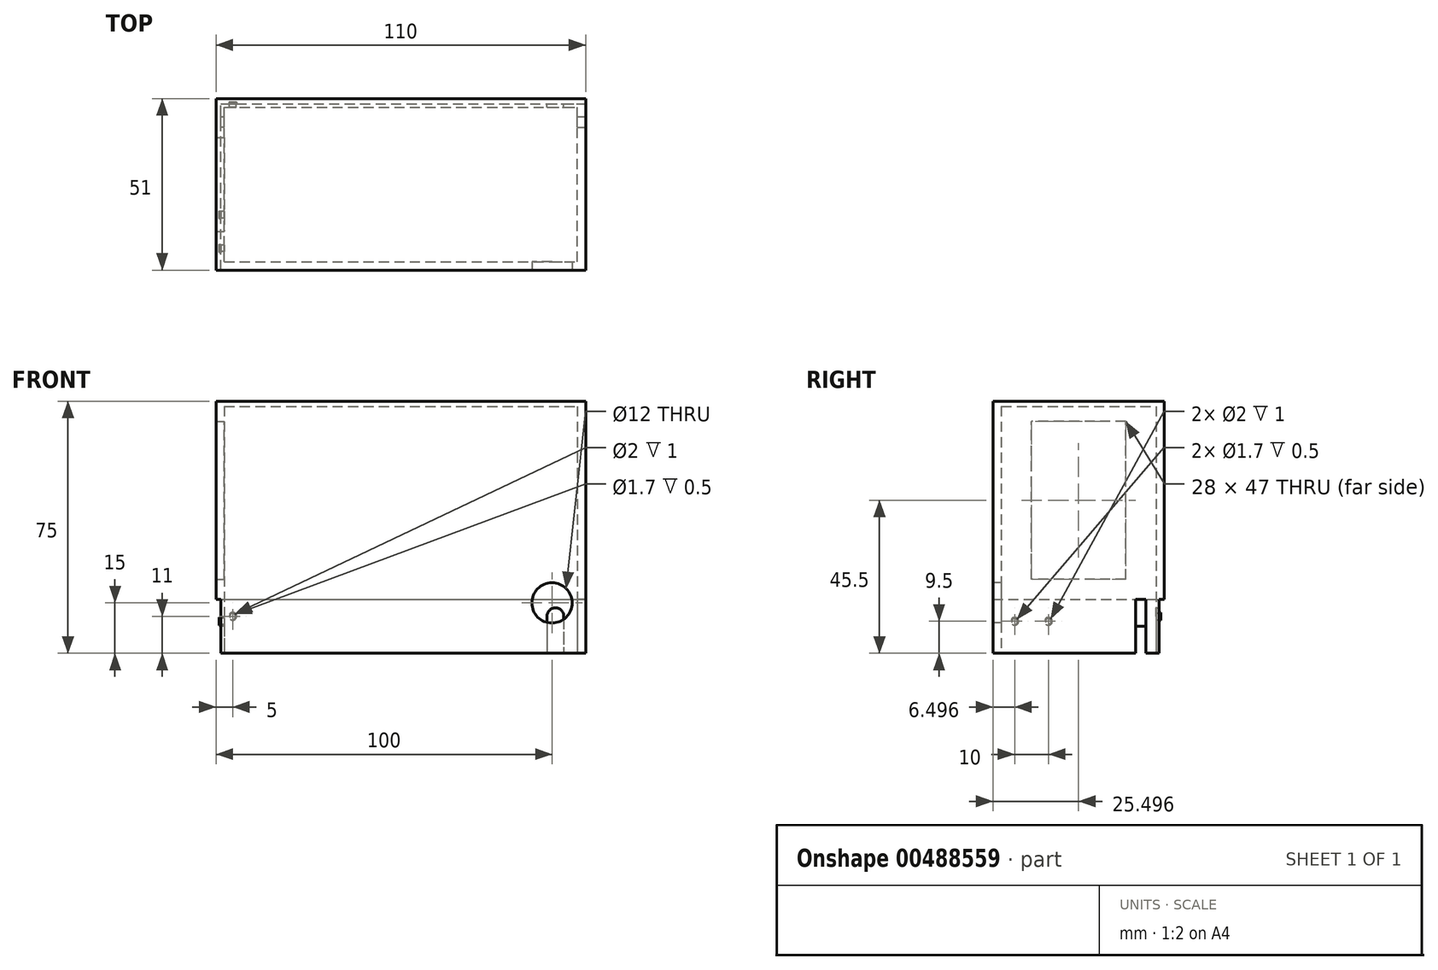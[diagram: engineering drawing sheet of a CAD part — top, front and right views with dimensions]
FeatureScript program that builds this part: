
annotation { "Feature Type Name" : "Feature", "Feature Type Description" : "" }
export const myFeature = defineFeature(function(context is Context, id is Id, definition is map)
    precondition{}
    {
        {
            var Q0;
            Q0=qCreatedBy(makeId("Top.planeOp"),FACE);
            var sketch = newSketch(context, id + "F0", { "sketchPlane" : qUnion([Q0])});
            skLineSegment(sketch, "E0.bottom", {"start": v(-40.86, -34.43) * mm, "end": v(69.14, -34.43) * mm});
            skLineSegment(sketch, "E0.top", {"start": v(-40.86, 16.57) * mm, "end": v(69.14, 16.57) * mm});
            skLineSegment(sketch, "E0.left", {"start": v(-40.86, -34.43) * mm, "end": v(-40.86, 16.57) * mm});
            skLineSegment(sketch, "E0.right", {"start": v(69.14, -34.43) * mm, "end": v(69.14, 16.57) * mm});
            skLineSegment(sketch, "E1.0", {"start": v(-38.36, -31.93) * mm, "end": v(-38.36, 14.07) * mm});
            skLineSegment(sketch, "E1.1", {"start": v(-38.36, -31.93) * mm, "end": v(66.64, -31.93) * mm});
            skLineSegment(sketch, "E1.2", {"start": v(66.64, -31.93) * mm, "end": v(66.64, 14.07) * mm});
            skLineSegment(sketch, "E1.3", {"start": v(-38.36, 14.07) * mm, "end": v(66.64, 14.07) * mm});
            skSolve(sketch);
        }
        {
            var Q0;
            Q0=makeQuery(id+"F0.imprint","IMPRINT",FACE,{"disambiguationData":[TD([[makeQuery(id+"F0.imprint","IMPRINT",EDGE,{"derivedFrom":sQuery(id+"F0.wireOp",EDGE,"E0.bottom")}),1.0]])]});
            extrude(context, id + "F1", {"entities" : qUnion([Q0]), "depth" : 75 * mm});
        }
        {
            var Q0;
            Q0=makeQuery(id+"F0.imprint","IMPRINT",FACE,{"disambiguationData":[TD([[makeQuery(id+"F0.imprint","IMPRINT",EDGE,{"derivedFrom":sQuery(id+"F0.wireOp",EDGE,"E0.bottom")}),1.0]])]});
            var sketch = newSketch(context, id + "F2", { "sketchPlane" : qUnion([Q0])});
            skLineSegment(sketch, "E2.0", {"start": v(-39.36, 15.07) * mm, "end": v(69.14, 15.07) * mm});
            skLineSegment(sketch, "E2.1", {"start": v(-39.36, -34.43) * mm, "end": v(-39.36, 15.07) * mm});
            skSolve(sketch);
        }
        {
            var Q0;
            {var subQ3=sQuery(id+"F2.wireOp",EDGE,"E2.0");Q0=makeQuery(id+"F2.imprint","IMPRINT",FACE,{"disambiguationData":[TD([[makeQuery(id+"F2.imprint","IMPRINT",EDGE,{"derivedFrom":subQ3}),1.0]])]});}
            extrude(context, id + "F3", {"entities" : qUnion([Q0]), "depth" : 16 * mm});
        }
        {
            var Q0;
            Q0=makeQuery(id+"F3.opExtrude","SWEPT_BODY",BODY,{"disambiguationData":[OSD([sQuery(id+"F0.wireOp",EDGE,"E0.bottom"),sQuery(id+"F0.wireOp",EDGE,"E0.top"),sQuery(id+"F0.wireOp",EDGE,"E0.left"),sQuery(id+"F0.wireOp",EDGE,"E0.right"),sQuery(id+"F2.wireOp",EDGE,"67fc0016-b919-42dd-8cfe-59e69e24b751.0"),sQuery(id+"F2.wireOp",EDGE,"67fc0016-b919-42dd-8cfe-59e69e24b751.1")])]});
            var Q1;
            Q1=makeQuery(id+"F1.opExtrude","SWEPT_BODY",BODY,{"disambiguationData":[OSD([sQuery(id+"F0.wireOp",EDGE,"E0.bottom"),sQuery(id+"F0.wireOp",EDGE,"E0.top"),sQuery(id+"F0.wireOp",EDGE,"E0.left"),sQuery(id+"F0.wireOp",EDGE,"E0.right"),sQuery(id+"F0.wireOp",EDGE,"E1.0"),sQuery(id+"F0.wireOp",EDGE,"E1.1"),sQuery(id+"F0.wireOp",EDGE,"E1.2"),sQuery(id+"F0.wireOp",EDGE,"E1.3")])]});
            booleanBodies(context, id + "F4", {"operationType" : BooleanOperationType.SUBTRACTION, "tools" : qUnion([Q0]), "targets" : qUnion([Q1])});
        }
        {
            var Q0;
            {var subQ1=sQuery(id+"F2.wireOp",EDGE,"E2.0");Q0=makeQuery(id+"F2.imprint","IMPRINT",FACE,{"disambiguationData":[TD([[makeQuery(id+"F2.imprint","IMPRINT",EDGE,{"derivedFrom":subQ1}),-1.0]])]});}
            var sketch = newSketch(context, id + "F5", { "sketchPlane" : qUnion([Q0])});
            skLineSegment(sketch, "E3", {"start": v(-38.36, 11.07) * mm, "end": v(-39.36, 11.07) * mm});
            skLineSegment(sketch, "E4", {"start": v(-38.36, 8.07) * mm, "end": v(-39.36, 8.07) * mm});
            skLineSegment(sketch, "E5", {"start": v(-39.36, 11.07) * mm, "end": v(-39.36, 8.07) * mm});
            skLineSegment(sketch, "E6", {"start": v(-38.36, 11.07) * mm, "end": v(-38.36, 8.07) * mm});
            skSolve(sketch);
        }
        {
            var Q0;
            Q0=makeQuery(id+"F5.imprint","IMPRINT",FACE,{"disambiguationData":[TD([[makeQuery(id+"F5.imprint","IMPRINT",EDGE,{"derivedFrom":sQuery(id+"F5.wireOp",EDGE,"E3")}),1.0]])]});
            extrude(context, id + "F6", {"entities" : qUnion([Q0]), "depth" : 8 * mm});
        }
        {
            var Q0;
            Q0=makeQuery(id+"F6.opExtrude","SWEPT_BODY",BODY,{"disambiguationData":[OSD([sQuery(id+"F5.wireOp",EDGE,"E3"),sQuery(id+"F5.wireOp",EDGE,"E4"),sQuery(id+"F5.wireOp",EDGE,"E5"),sQuery(id+"F5.wireOp",EDGE,"E6")])]});
            var Q1;
            Q1=makeQuery(id+"F1.opExtrude","SWEPT_BODY",BODY,{"disambiguationData":[OSD([sQuery(id+"F0.wireOp",EDGE,"E0.bottom"),sQuery(id+"F0.wireOp",EDGE,"E0.top"),sQuery(id+"F0.wireOp",EDGE,"E0.left"),sQuery(id+"F0.wireOp",EDGE,"E0.right"),sQuery(id+"F0.wireOp",EDGE,"E1.0"),sQuery(id+"F0.wireOp",EDGE,"E1.1"),sQuery(id+"F0.wireOp",EDGE,"E1.2"),sQuery(id+"F0.wireOp",EDGE,"E1.3")])]});
            booleanBodies(context, id + "F7", {"operationType" : BooleanOperationType.SUBTRACTION, "tools" : qUnion([Q0]), "targets" : qUnion([Q1])});
        }
        {
            var Q0;
            Q0=makeQuery(id+"F0.imprint","IMPRINT",FACE,{"disambiguationData":[TD([[makeQuery(id+"F0.imprint","IMPRINT",EDGE,{"derivedFrom":sQuery(id+"F0.wireOp",EDGE,"E0.bottom")}),1.0]])]});
            var sketch = newSketch(context, id + "F8", { "sketchPlane" : qUnion([Q0])});
            skLineSegment(sketch, "E7", {"start": v(-38.86, 11.07) * mm, "end": v(69.14, 11.07) * mm, "construction": true});
            skLineSegment(sketch, "E8", {"start": v(-39.36, 8.07) * mm, "end": v(69.14, 8.07) * mm, "construction": true});
            skLineSegment(sketch, "E9", {"start": v(69.14, 11.07) * mm, "end": v(66.64, 11.07) * mm});
            skLineSegment(sketch, "E10", {"start": v(66.64, 11.07) * mm, "end": v(66.64, 8.07) * mm});
            skLineSegment(sketch, "E11", {"start": v(66.64, 8.07) * mm, "end": v(69.14, 8.07) * mm});
            skLineSegment(sketch, "E12", {"start": v(69.14, 11.07) * mm, "end": v(69.14, 8.07) * mm});
            skSolve(sketch);
        }
        {
            var Q0;
            Q0 = qSketchRegion(id + "F8", true);
            extrude(context, id + "F9", {"entities" : qUnion([Q0]), "depth" : 16 * mm});
        }
        {
            var Q0;
            Q0=makeQuery(id+"F9.opExtrude","SWEPT_BODY",BODY,{"disambiguationData":[OSD([sQuery(id+"F8.wireOp",EDGE,"E9"),sQuery(id+"F8.wireOp",EDGE,"E10"),sQuery(id+"F8.wireOp",EDGE,"E11"),sQuery(id+"F8.wireOp",EDGE,"E12")])]});
            var Q1;
            Q1=makeQuery(id+"F1.opExtrude","SWEPT_BODY",BODY,{"disambiguationData":[OSD([sQuery(id+"F0.wireOp",EDGE,"E0.bottom"),sQuery(id+"F0.wireOp",EDGE,"E0.top"),sQuery(id+"F0.wireOp",EDGE,"E0.left"),sQuery(id+"F0.wireOp",EDGE,"E0.right"),sQuery(id+"F0.wireOp",EDGE,"E1.0"),sQuery(id+"F0.wireOp",EDGE,"E1.1"),sQuery(id+"F0.wireOp",EDGE,"E1.2"),sQuery(id+"F0.wireOp",EDGE,"E1.3")])]});
            booleanBodies(context, id + "F10", {"operationType" : BooleanOperationType.SUBTRACTION, "tools" : qUnion([Q0]), "targets" : qUnion([Q1])});
        }
        {
            var Q0;
            Q0=makeQuery(id+"F1.opExtrude","SWEPT_FACE",FACE,{"disambiguationData":[OSD([sQuery(id+"F0.wireOp",EDGE,"E1.3")])]});
            var sketch = newSketch(context, id + "F11", { "sketchPlane" : qUnion([Q0])});
            skCircle(sketch, "E13", {"center": v(60.14, 11) * mm, "radius": 2.5 * mm});
            skLineSegment(sketch, "E14", {"start": v(60.14, 11) * mm, "end": v(60.14, 0) * mm, "construction": true});
            skLineSegment(sketch, "E15", {"start": v(62.64, 11) * mm, "end": v(62.64, 0) * mm});
            skLineSegment(sketch, "E16", {"start": v(60.14, 11) * mm, "end": v(66.64, 11) * mm, "construction": true});
            skLineSegment(sketch, "E17", {"start": v(57.64, 11) * mm, "end": v(57.64, 0) * mm});
            skSolve(sketch);
        }
        {
            var Q0;
            {var subQ0=sQuery(id+"F11.wireOp",EDGE,"E15");Q0=makeQuery(id+"F11.imprint","IMPRINT",FACE,{"disambiguationData":[TD([[makeQuery(id+"F11.imprint","IMPRINT",EDGE,{"derivedFrom":subQ0}),-1.0]])]});}
            var Q1;
            {var subQ0=sQuery(id+"F11.wireOp",EDGE,"E13");var subQ1=makeQuery(id+"F11.imprint","INTERSECT",VERTEX,{"derivedFrom":[subQ0,sQuery(id+"F11.wireOp",EDGE,"E15")]});Q1=makeQuery(id+"F11.imprint","IMPRINT",FACE,{"disambiguationData":[TD([[makeQuery(id+"F11.imprint","IMPRINT",EDGE,{"disambiguationData":[TD([[subQ1,1.0]])],"derivedFrom":subQ0}),1.0]])]});}
            extrude(context, id + "F12", {"entities" : qUnion([Q0, Q1]), "endBound" : BoundingType.SYMMETRIC, "depth" : 10 * mm});
        }
        {
            var Q0;
            Q0=makeQuery(id+"F12.opExtrude","SWEPT_BODY",BODY,{"disambiguationData":[OSD([sQuery(id+"F0.wireOp",EDGE,"E0.bottom"),sQuery(id+"F0.wireOp",EDGE,"E0.top"),sQuery(id+"F0.wireOp",EDGE,"E0.left"),sQuery(id+"F0.wireOp",EDGE,"E0.right"),sQuery(id+"F0.wireOp",EDGE,"E1.0"),sQuery(id+"F0.wireOp",EDGE,"E1.1"),sQuery(id+"F0.wireOp",EDGE,"E1.2"),sQuery(id+"F0.wireOp",EDGE,"E1.3"),sQuery(id+"F2.wireOp",EDGE,"E2.0"),sQuery(id+"FzfTKWj9B2n3RX8_1.wireOp",EDGE,"ftydJ3Cq-NlXn-dJUW-CoY5-lXdrAIjHJlYn"),sQuery(id+"FzfTKWj9B2n3RX8_1.wireOp",EDGE,"CNzBpTfi-9pIe-DhWO-TU5M-x5CUNgwVa0qN"),sQuery(id+"FzfTKWj9B2n3RX8_1.wireOp",EDGE,"677467ae-143c-4d0b-99db-88d1016388af0.MirrorCS")])]});
            var Q1;
            Q1=makeQuery(id+"F1.opExtrude","SWEPT_BODY",BODY,{"disambiguationData":[OSD([sQuery(id+"F0.wireOp",EDGE,"E0.bottom"),sQuery(id+"F0.wireOp",EDGE,"E0.top"),sQuery(id+"F0.wireOp",EDGE,"E0.left"),sQuery(id+"F0.wireOp",EDGE,"E0.right"),sQuery(id+"F0.wireOp",EDGE,"E1.0"),sQuery(id+"F0.wireOp",EDGE,"E1.1"),sQuery(id+"F0.wireOp",EDGE,"E1.2"),sQuery(id+"F0.wireOp",EDGE,"E1.3")])]});
            booleanBodies(context, id + "F13", {"operationType" : BooleanOperationType.SUBTRACTION, "tools" : qUnion([Q0]), "targets" : qUnion([Q1])});
        }
        {
            var Q0;
            Q0=makeQuery(id+"F4.opBoolean","COPY",FACE,{"derivedFrom":makeQuery(id+"F3.opExtrude","SWEPT_FACE",FACE,{"disambiguationData":[OSD([sQuery(id+"F2.wireOp",EDGE,"E2.1")])]})});
            var sketch = newSketch(context, id + "F14", { "sketchPlane" : qUnion([Q0])});
            skCircle(sketch, "E18", {"center": v(27.93, 9.5) * mm, "radius": 1.15 * mm});
            skCircle(sketch, "E19", {"center": v(17.93, 9.5) * mm, "radius": 1.15 * mm});
            skCircle(sketch, "E20.0", {"center": v(27.93, 9.5) * mm, "radius": 0.85 * mm});
            skCircle(sketch, "E21.0", {"center": v(17.93, 9.5) * mm, "radius": 0.85 * mm});
            skLineSegment(sketch, "E22", {"start": v(17.93, 9.5) * mm, "end": v(17.93, 16) * mm, "construction": true});
            skLineSegment(sketch, "E23", {"start": v(27.93, 9.5) * mm, "end": v(27.93, 16) * mm, "construction": true});
            skSolve(sketch);
        }
        {
            var Q0;
            Q0=sQuery(id+"F14.wireOp",VERTEX,"hwPzBVvx-uJ7I-B0q1-T1zj-nQxkntDnHqa2.center");
            var Q1;
            Q1=sQuery(id+"F14.wireOp",VERTEX,"E18.center");
            var Q2;
            Q2=sQuery(id+"F14.wireOp",VERTEX,"E21.0.center");
            var Q3;
            Q3=makeQuery(id+"F1.opExtrude","SWEPT_BODY",BODY,{"disambiguationData":[OSD([sQuery(id+"F0.wireOp",EDGE,"E0.bottom"),sQuery(id+"F0.wireOp",EDGE,"E0.top"),sQuery(id+"F0.wireOp",EDGE,"E0.left"),sQuery(id+"F0.wireOp",EDGE,"E0.right"),sQuery(id+"F0.wireOp",EDGE,"E1.0"),sQuery(id+"F0.wireOp",EDGE,"E1.1"),sQuery(id+"F0.wireOp",EDGE,"E1.2"),sQuery(id+"F0.wireOp",EDGE,"E1.3")])]});
            hole(context, id + "F15", {"style" : HoleStyle.SIMPLE, "endStyle" : HoleEndStyle.BLIND, "holeDiameter" : 2 * mm, "holeDepth" : 12 * mm, "isTappedThrough" : true, "tappedDepth" : 12 * mm, "tapClearance" : 3, "locations" : qUnion([Q0, Q1, Q2]), "scope" : qUnion([Q3])});
        }
        {
            var Q0;
            Q0=makeQuery(id+"F1.opExtrude","SWEPT_FACE",FACE,{"disambiguationData":[OSD([sQuery(id+"F0.wireOp",EDGE,"E0.left")])]});
            var sketch = newSketch(context, id + "F16", { "sketchPlane" : qUnion([Q0])});
            skLineSegment(sketch, "E24.bottom", {"start": v(22.93, 69) * mm, "end": v(-5.07, 69) * mm});
            skLineSegment(sketch, "E24.top", {"start": v(22.93, 22) * mm, "end": v(-5.07, 22) * mm});
            skLineSegment(sketch, "E24.left", {"start": v(22.93, 69) * mm, "end": v(22.93, 22) * mm});
            skLineSegment(sketch, "E24.right", {"start": v(-5.07, 69) * mm, "end": v(-5.07, 22) * mm});
            skPoint(sketch, "E24.middle", {"position": v(8.93, 45.5) * mm});
            skLineSegment(sketch, "E25", {"start": v(-16.57, 45.5) * mm, "end": v(34.43, 45.5) * mm, "construction": true});
            skSolve(sketch);
        }
        {
            var Q0;
            Q0=makeQuery(id+"F16.imprint","IMPRINT",FACE,{"disambiguationData":[TD([[makeQuery(id+"F16.imprint","IMPRINT",EDGE,{"derivedFrom":sQuery(id+"F16.wireOp",EDGE,"E24.bottom")}),1.0]])]});
            extrude(context, id + "F17", {"entities" : qUnion([Q0]), "endBound" : BoundingType.SYMMETRIC, "depth" : 25 * mm});
        }
        {
            var Q0;
            Q0=makeQuery(id+"F17.opExtrude","SWEPT_BODY",BODY,{"disambiguationData":[OSD([sQuery(id+"F16.wireOp",EDGE,"E24.bottom"),sQuery(id+"F16.wireOp",EDGE,"E24.top"),sQuery(id+"F16.wireOp",EDGE,"E24.left"),sQuery(id+"F16.wireOp",EDGE,"E24.right")])]});
            var Q1;
            Q1=makeQuery(id+"F1.opExtrude","SWEPT_BODY",BODY,{"disambiguationData":[OSD([sQuery(id+"F0.wireOp",EDGE,"E0.bottom"),sQuery(id+"F0.wireOp",EDGE,"E0.top"),sQuery(id+"F0.wireOp",EDGE,"E0.left"),sQuery(id+"F0.wireOp",EDGE,"E0.right"),sQuery(id+"F0.wireOp",EDGE,"E1.0"),sQuery(id+"F0.wireOp",EDGE,"E1.1"),sQuery(id+"F0.wireOp",EDGE,"E1.2"),sQuery(id+"F0.wireOp",EDGE,"E1.3")])]});
            booleanBodies(context, id + "F18", {"operationType" : BooleanOperationType.SUBTRACTION, "tools" : qUnion([Q0]), "targets" : qUnion([Q1])});
        }
        {
            var Q0;
            Q0=makeQuery(id+"F1.opExtrude","CAP_FACE",FACE,{"disambiguationData":[OSD([sQuery(id+"F0.wireOp",EDGE,"E0.bottom"),sQuery(id+"F0.wireOp",EDGE,"E0.top"),sQuery(id+"F0.wireOp",EDGE,"E0.left"),sQuery(id+"F0.wireOp",EDGE,"E0.right"),sQuery(id+"F0.wireOp",EDGE,"E1.0"),sQuery(id+"F0.wireOp",EDGE,"E1.1"),sQuery(id+"F0.wireOp",EDGE,"E1.2"),sQuery(id+"F0.wireOp",EDGE,"E1.3")])],"isStart":false});
            var sketch = newSketch(context, id + "F19", { "sketchPlane" : qUnion([Q0])});
            skSolve(sketch);
        }
        {
            var Q0;
            Q0=makeQuery(id+"F19.imprint","IMPRINT",FACE,{"disambiguationData":[TD([[makeQuery(id+"F19.imprint","IMPRINT",EDGE,{"derivedFrom":makeQuery(id+"F1.opExtrude","CAP_EDGE",EDGE,{"disambiguationData":[OSD([sQuery(id+"F0.wireOp",EDGE,"E1.0")])],"isStart":false})}),-1.0]])]});
            extrude(context, id + "F20", {"entities" : qUnion([Q0]), "operationType" : NewBodyOperationType.ADD, "oppositeDirection" : true, "depth" : 1.5 * mm});
        }
        {
            var Q0;
            Q0=makeQuery(id+"F1.opExtrude","SWEPT_FACE",FACE,{"disambiguationData":[OSD([sQuery(id+"F0.wireOp",EDGE,"E0.bottom")])]});
            var sketch = newSketch(context, id + "F21", { "sketchPlane" : qUnion([Q0])});
            skPoint(sketch, "E26", {"position": v(59.14, 15) * mm});
            skSolve(sketch);
        }
        {
            var Q0;
            Q0=sQuery(id+"F21.wireOp",VERTEX,"E26");
            var Q1;
            Q1=makeQuery(id+"F1.opExtrude","SWEPT_BODY",BODY,{"disambiguationData":[OSD([sQuery(id+"F0.wireOp",EDGE,"E0.bottom"),sQuery(id+"F0.wireOp",EDGE,"E0.top"),sQuery(id+"F0.wireOp",EDGE,"E0.left"),sQuery(id+"F0.wireOp",EDGE,"E0.right"),sQuery(id+"F0.wireOp",EDGE,"E1.0"),sQuery(id+"F0.wireOp",EDGE,"E1.1"),sQuery(id+"F0.wireOp",EDGE,"E1.2"),sQuery(id+"F0.wireOp",EDGE,"E1.3")])]});
            hole(context, id + "F22", {"style" : HoleStyle.SIMPLE, "endStyle" : HoleEndStyle.BLIND, "holeDiameter" : 12 * mm, "holeDepth" : 12 * mm, "isTappedThrough" : true, "tappedDepth" : 12 * mm, "tapClearance" : 3, "locations" : qUnion([Q0]), "scope" : qUnion([Q1])});
        }
        {
            var Q0;
            Q0 = qSketchRegion(id + "F14", true);
            var Q1;
            Q1 = qSketchRegion(id + "F24", true);
            extrude(context, id + "F23", {"entities" : qUnion([Q0, Q1]), "operationType" : NewBodyOperationType.ADD, "depth" : 0.5 * mm});
        }
        {
            var Q0;
            Q0=makeQuery(id+"F4.opBoolean","COPY",FACE,{"derivedFrom":makeQuery(id+"F3.opExtrude","SWEPT_FACE",FACE,{"disambiguationData":[OSD([sQuery(id+"F2.wireOp",EDGE,"E2.0")])]})});
            var sketch = newSketch(context, id + "F24", { "sketchPlane" : qUnion([Q0])});
            skCircle(sketch, "E27", {"center": v(35.86, 11) * mm, "radius": 1.15 * mm});
            skLineSegment(sketch, "E28", {"start": v(35.86, 11) * mm, "end": v(39.36, 11) * mm, "construction": true});
            skCircle(sketch, "E29.0", {"center": v(35.86, 11) * mm, "radius": 0.85 * mm});
            skSolve(sketch);
        }
        {
            var Q0;
            Q0=sQuery(id+"F24.wireOp",VERTEX,"E28.start");
            var Q1;
            Q1=makeQuery(id+"F1.opExtrude","SWEPT_BODY",BODY,{"disambiguationData":[OSD([sQuery(id+"F0.wireOp",EDGE,"E0.bottom"),sQuery(id+"F0.wireOp",EDGE,"E0.top"),sQuery(id+"F0.wireOp",EDGE,"E0.left"),sQuery(id+"F0.wireOp",EDGE,"E0.right"),sQuery(id+"F0.wireOp",EDGE,"E1.0"),sQuery(id+"F0.wireOp",EDGE,"E1.1"),sQuery(id+"F0.wireOp",EDGE,"E1.2"),sQuery(id+"F0.wireOp",EDGE,"E1.3")])]});
            hole(context, id + "F25", {"style" : HoleStyle.SIMPLE, "endStyle" : HoleEndStyle.BLIND, "holeDiameter" : 2 * mm, "holeDepth" : 12 * mm, "isTappedThrough" : true, "tappedDepth" : 12 * mm, "tapClearance" : 3, "locations" : qUnion([Q0]), "scope" : qUnion([Q1])});
        }
        {
            var Q0;
            Q0 = qSketchRegion(id + "F24", true);
            extrude(context, id + "F26", {"entities" : qUnion([Q0]), "operationType" : NewBodyOperationType.ADD, "depth" : 0.5 * mm});
        }
    });
